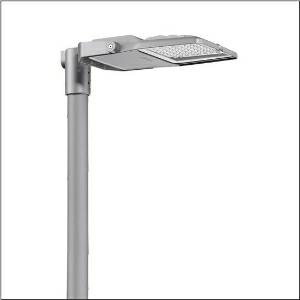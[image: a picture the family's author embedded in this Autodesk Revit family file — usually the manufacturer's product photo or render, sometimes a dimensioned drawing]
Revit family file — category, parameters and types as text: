
# Revit family: floodlight_fl_21_iq_mini___pl61_5xa7772c2c3a_f769
name_source: partatom
category: Lighting Fixtures
units: mm (PartAtom-declared; Revit-internal decimal feet)

## family parameters
Cut with Voids When Loaded = No
Host = Face
Light Source = No
Part Type = Normal
Room Calculation Point = No
Round Connector Dimension = Use Diameter
Shared = No

## types (1)
- --- (1 x LED, 11980 lm, 87.2 W, 3000K)
    Apparent Load = 87 VA
    CIE Flux Codes = 33 65 98 100 100
    Color Rendering = 70
    Color Temperature = 3000K
    Default Elevation = 1800 mm
    Description = Floodlight FL 21 iQ mini, floodlight, primary light control with lens, of PMMA, primary optical cover: protective disc, of toughened safety glass, transparent, light distribution: PL61, light emission: direct distribution, installation type: surface-mounted, lamps: LED, High Power LED, rated values: 11.980lm | 87,2W | 137,4lm/W (begin service life); end service life: 11.980lm | 92,1W; at 50% lumin. flux: 5.990lm | 40,1W | 149,4lm/W, colour temperature: 3000K, colour rendering: CRI > 70, light colour: 730, light setting 1 begin service life: 100% | 11.980lm | 87,2W | 137,4lm/W | 3.000K, light setting 1 end service life: 92,1W, further light settings possible, control: pre-setting: linear dimming characteristic, Auto-Match, Temp-Guard, Night-Set, Smart-Wire, Desk-Remote (wireless, voltage-free reading and setting of iQ features in the workshop via application-optimized NFC function/RFID function), optimised constant luminous flux control (CLO 2.0), Light-Fading, Lumen-Switch, with terminal, 6-pole, mains connection: 220..240V, AC, 50/60Hz, luminaire housing, of diecast aluminium, powder-coated, SITECO metallic grey (DB 702S), corrosivity category C5 mid according to DIN EN ISO 12944suitable for swimming poolschlorine-resistant, sealing non-destructively replaceable, please order mast flange separately, mast bracket, of steel, galvanised, powder-coated, protection rating (complete): IP66, insulation class (complete): insulation class II (safety insulation), certification: CE, ENEC, VDE, protection symbol: D, impact resistance: IK08, permissible operating ambient temperature: -40..+40°C, permissible operating ambient temperature for outdoor applications: -40..+50°C, standard: DIN EN 12944, LABS conformity tested according to VDMA 24364:2018-05, packaging unit: 1 piece

Light Distribution: PL61
    Height = 70 mm
    Lamp = 1 x LED
    Lamp Light Flux = 11980 lm
    Lamp Power = 87.2 W
    Lamp count = 1
    Length = 485 mm
    Luminous efficacy = 137 lm/W
    Manufacturer = Siteco
    ModVariant = No
    Model = 5XA7772C2C3A
    Number of Poles = 1
    OnlyDefault = Yes
    Power Factor = 1
    Product Name = Floodlight FL 21 iQ mini | PL61
    Product group = floodlight | pylon annexe
    ProductGroupID = 6201
    Protection Class = Protection class II
    Protection Degree = IP 66
    RLX_Detail_Level = 1
    RLX_Emergency_Light_Flux = 0 lm
    RLX_Emergency_Type = 0
    RLX_Emergency_Type_DB = No
    RlxData = <blob elided: 101685 chars, md5=53a32f2c>
    Socket = socket
    Standby Power = 0 W
    System Light Flux = 11980 lm
    System Power = 87 W
    Type Comments = factory setting: luminous flux: 100 % | dim-lin: 254 | 456 mA
    Type Image = l_1007125.jpg
    URL = http://relux.com
    VarID = @adj_172529
    Voltage = 0 V
    Weight = 0.00 kg
    Width = 337 mm

## geometry (parser evidence)
native form markers: Blend x4, Sweep x11
no freeform markers — native parametric forms only
